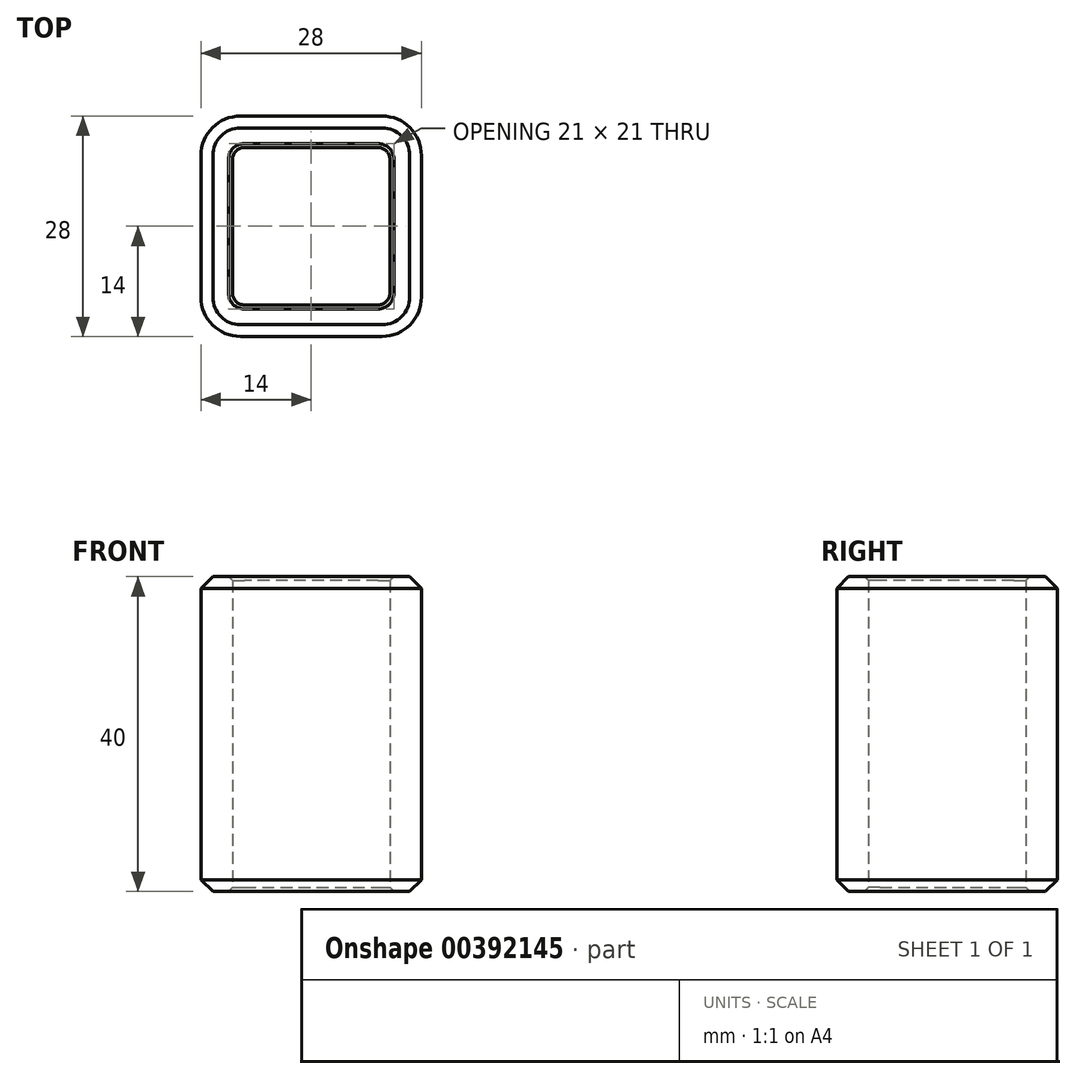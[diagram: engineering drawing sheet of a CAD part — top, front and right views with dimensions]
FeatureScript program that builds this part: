
annotation { "Feature Type Name" : "Feature", "Feature Type Description" : "" }
export const myFeature = defineFeature(function(context is Context, id is Id, definition is map)
    precondition{}
    {
        {
            var Q0;
            Q0=qCreatedBy(makeId("Top.planeOp"),FACE);
            var sketch = newSketch(context, id + "F0", { "sketchPlane" : qUnion([Q0])});
            skLineSegment(sketch, "E0.bottom", {"start": v(-10, 10) * mm, "end": v(10, 10) * mm});
            skLineSegment(sketch, "E0.top", {"start": v(-10, -10) * mm, "end": v(10, -10) * mm});
            skLineSegment(sketch, "E0.left", {"start": v(-10, 10) * mm, "end": v(-10, -10) * mm});
            skLineSegment(sketch, "E0.right", {"start": v(10, 10) * mm, "end": v(10, -10) * mm});
            skLineSegment(sketch, "E1.bottom", {"start": v(-14, 14) * mm, "end": v(14, 14) * mm});
            skLineSegment(sketch, "E1.top", {"start": v(-14, -14) * mm, "end": v(14, -14) * mm});
            skLineSegment(sketch, "E1.left", {"start": v(-14, 14) * mm, "end": v(-14, -14) * mm});
            skLineSegment(sketch, "E1.right", {"start": v(14, 14) * mm, "end": v(14, -14) * mm});
            skSolve(sketch);
        }
        {
            var Q0;
            Q0 = qSketchRegion(id + "F0", true);
            extrude(context, id + "F1", {"entities" : qUnion([Q0]), "depth" : 40 * mm});
        }
        {
            var Q0;
            Q0=makeQuery(id+"F1.opExtrude","SWEPT_EDGE",EDGE,{"disambiguationData":[OSD([sQuery(id+"F0.wireOp",EDGE,"E0.bottom"),sQuery(id+"F0.wireOp",EDGE,"E0.left")])]});
            var Q1;
            Q1=makeQuery(id+"F1.opExtrude","SWEPT_EDGE",EDGE,{"disambiguationData":[OSD([sQuery(id+"F0.wireOp",EDGE,"E0.bottom"),sQuery(id+"F0.wireOp",EDGE,"E0.right")])]});
            var Q2;
            Q2=makeQuery(id+"F1.opExtrude","SWEPT_EDGE",EDGE,{"disambiguationData":[OSD([sQuery(id+"F0.wireOp",EDGE,"E0.top"),sQuery(id+"F0.wireOp",EDGE,"E0.right")])]});
            var Q3;
            Q3=makeQuery(id+"F1.opExtrude","SWEPT_EDGE",EDGE,{"disambiguationData":[OSD([sQuery(id+"F0.wireOp",EDGE,"E0.top"),sQuery(id+"F0.wireOp",EDGE,"E0.left")])]});
            fillet(context, id + "F2", {"entities" : qUnion([Q0, Q1, Q2, Q3]), "radius" : 1.5 * mm, "tangentPropagation" : true, "allowEdgeOverflow" : false});
        }
        {
            var Q0;
            Q0=makeQuery(id+"F1.opExtrude","SWEPT_EDGE",EDGE,{"disambiguationData":[OSD([sQuery(id+"F0.wireOp",EDGE,"E1.bottom"),sQuery(id+"F0.wireOp",EDGE,"E1.left")])]});
            var Q1;
            Q1=makeQuery(id+"F1.opExtrude","SWEPT_EDGE",EDGE,{"disambiguationData":[OSD([sQuery(id+"F0.wireOp",EDGE,"E1.top"),sQuery(id+"F0.wireOp",EDGE,"E1.left")])]});
            var Q2;
            Q2=makeQuery(id+"F1.opExtrude","SWEPT_EDGE",EDGE,{"disambiguationData":[OSD([sQuery(id+"F0.wireOp",EDGE,"E1.top"),sQuery(id+"F0.wireOp",EDGE,"E1.right")])]});
            var Q3;
            Q3=makeQuery(id+"F1.opExtrude","SWEPT_EDGE",EDGE,{"disambiguationData":[OSD([sQuery(id+"F0.wireOp",EDGE,"E1.bottom"),sQuery(id+"F0.wireOp",EDGE,"E1.right")])]});
            fillet(context, id + "F3", {"entities" : qUnion([Q0, Q1, Q2, Q3]), "radius" : 5 * mm, "tangentPropagation" : true, "allowEdgeOverflow" : false});
        }
        {
            var Q0;
            Q0=makeQuery(id+"F1.opExtrude","CAP_EDGE",EDGE,{"disambiguationData":[OSD([sQuery(id+"F0.wireOp",EDGE,"E1.left")])],"isStart":false});
            var Q1;
            Q1=makeQuery(id+"F1.opExtrude","CAP_EDGE",EDGE,{"disambiguationData":[OSD([sQuery(id+"F0.wireOp",EDGE,"E1.left")])],"isStart":true});
            chamfer(context, id + "F4", {"entities" : qUnion([Q0, Q1]), "width" : 1.5 * mm, "tangentPropagation" : true});
        }
        {
            var Q0;
            Q0=makeQuery(id+"F1.opExtrude","CAP_EDGE",EDGE,{"disambiguationData":[OSD([sQuery(id+"F0.wireOp",EDGE,"E0.left")])],"isStart":false});
            var Q1;
            Q1=makeQuery(id+"F1.opExtrude","CAP_EDGE",EDGE,{"disambiguationData":[OSD([sQuery(id+"F0.wireOp",EDGE,"E0.top")])],"isStart":true});
            chamfer(context, id + "F5", {"entities" : qUnion([Q0, Q1]), "width" : 0.5 * mm, "tangentPropagation" : true});
        }
    });
